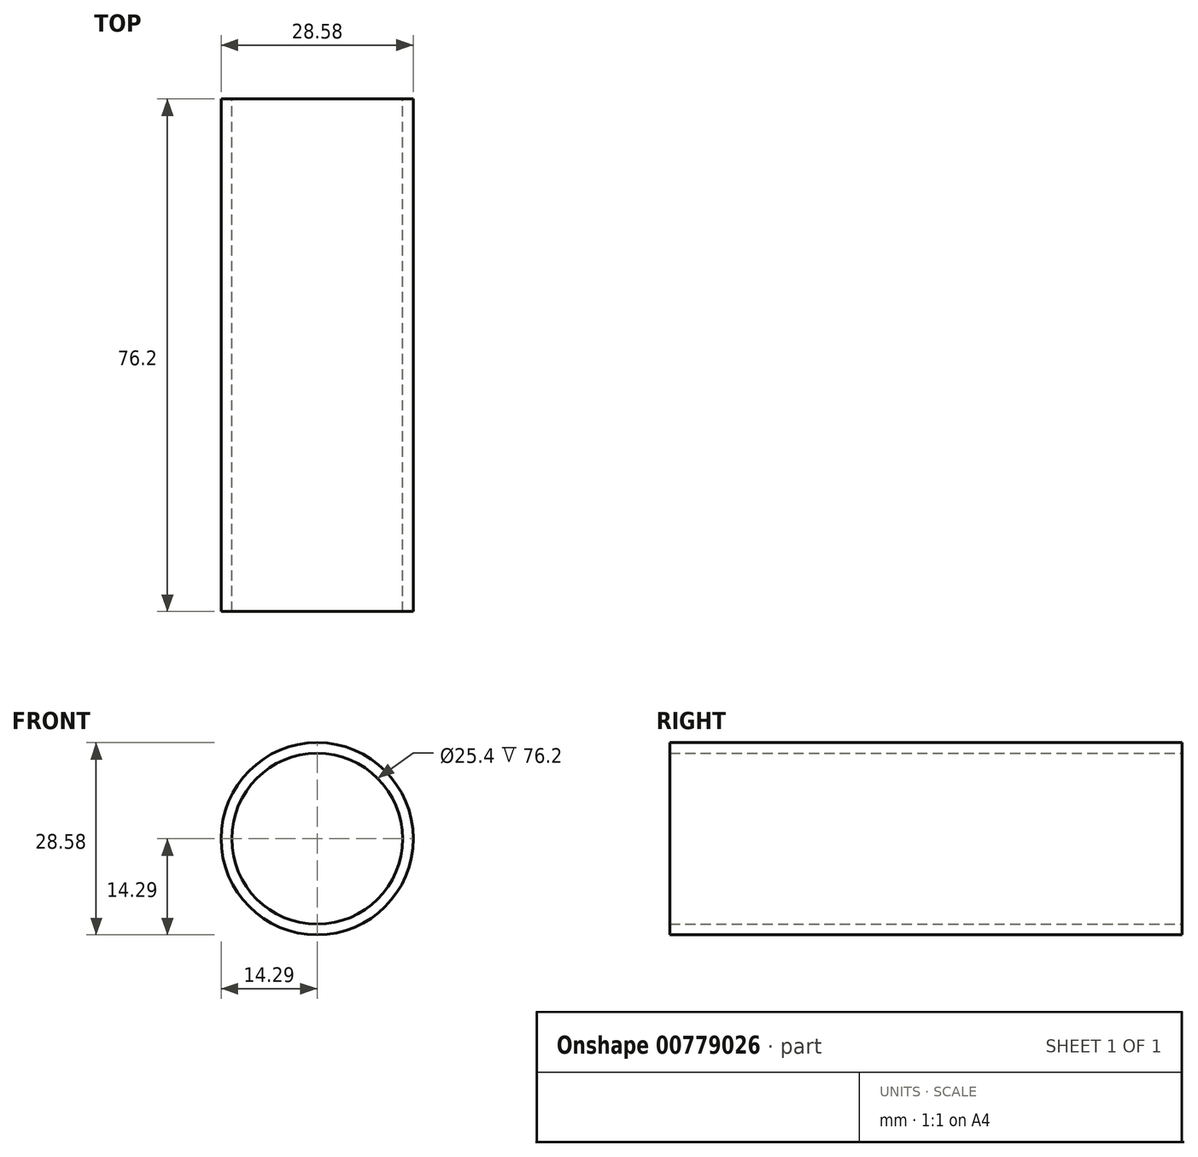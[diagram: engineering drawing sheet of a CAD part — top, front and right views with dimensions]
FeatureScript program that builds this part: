
annotation { "Feature Type Name" : "Feature", "Feature Type Description" : "" }
export const myFeature = defineFeature(function(context is Context, id is Id, definition is map)
    precondition{}
    {
        {
            var Q0;
            Q0=qCreatedBy(makeId("Front.planeOp"),FACE);
            var sketch = newSketch(context, id + "F0", { "sketchPlane" : qUnion([Q0])});
            skCircle(sketch, "E0", {"center": v(0, 0) * mm, "radius": 14.29 * mm});
            skCircle(sketch, "E1", {"center": v(0, 0) * mm, "radius": 12.7 * mm});
            skSolve(sketch);
        }
        {
            var Q0;
            Q0 = qSketchRegion(id + "F0", true);
            extrude(context, id + "F1", {"entities" : qUnion([Q0]), "depth" : 76.2 * mm, "offsetDistance" : 25.4 * mm});
        }
    });
